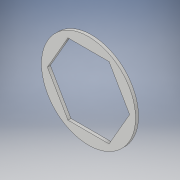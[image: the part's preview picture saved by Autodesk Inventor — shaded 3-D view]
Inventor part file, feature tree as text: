
AUTODESK INVENTOR PART (.ipt)
format: ipt  version: 2018 (Build 220112000, 112)  size: 103,424 bytes
history: native  units: in
note: dims shown in document units (in); Inventor stores cm internally (conversion verified against a paired STEP export)
features: extrude x1, sketch x1
ambient origin geometry x8: Origin, YZ Plane, XZ Plane, XY Plane, X Axis, Y Axis, Z Axis, Center Point
bodies: Solid1 (feature_tree)
feature tree (2):
  extrude  "Extrusion1"  Depth=0.021in
  sketch  "Sketch1"  dims[d0=0.5in d1=0.66in d2=0.021in d3=0.0in]
